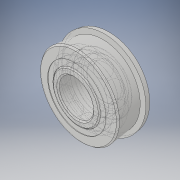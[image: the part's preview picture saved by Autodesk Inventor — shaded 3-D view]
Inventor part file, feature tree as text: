
AUTODESK INVENTOR PART (.ipt)
format: ipt  version: 2019 (Build 230136000, 136)  size: 627,712 bytes
history: native  units: in
note: dims shown in document units (in); Inventor stores cm internally (conversion verified against a paired STEP export)
features: other x11, revolve x5
ambient origin geometry x8: Origin, YZ Plane, XZ Plane, XY Plane, X Axis, Y Axis, Z Axis, Center Point
bodies: Solid1 (feature_tree), Solid2 (feature_tree), Solid3 (feature_tree), Solid4 (feature_tree), Solid5 (feature_tree), Solid6 (feature_tree), Solid7 (feature_tree), Solid8 (feature_tree), Solid9 (feature_tree), Solid10 (feature_tree), Solid11 (feature_tree), Solid12 (feature_tree), Solid13 (feature_tree), Solid14 (feature_tree), Solid15 (feature_tree), Solid16 (feature_tree)
feature tree (16):
  revolve  "Revolve3"  [1 undecoded]
  revolve  "Revolve4"  [1 undecoded]
  other  "CirPattern1[1]"
  other  "CirPattern1[2]"
  other  "CirPattern1[3]"
  other  "CirPattern1[4]"
  other  "CirPattern1[5]"
  other  "CirPattern1[6]"
  other  "CirPattern1[7]"
  other  "CirPattern1[8]"
  other  "CirPattern1[9]"
  other  "CirPattern1[10]"
  other  "CirPattern1[11]"
  revolve  "Revolve5[1]"  [1 undecoded]
  revolve  "Revolve5[2]"  [1 undecoded]
  revolve  "Revolve6"  [1 undecoded]
note: 5 required parameter values undecoded (feature->parameter linkage not recoverable at this tier; creation-order binding heuristic only, values carry confidence <= 0.55)
